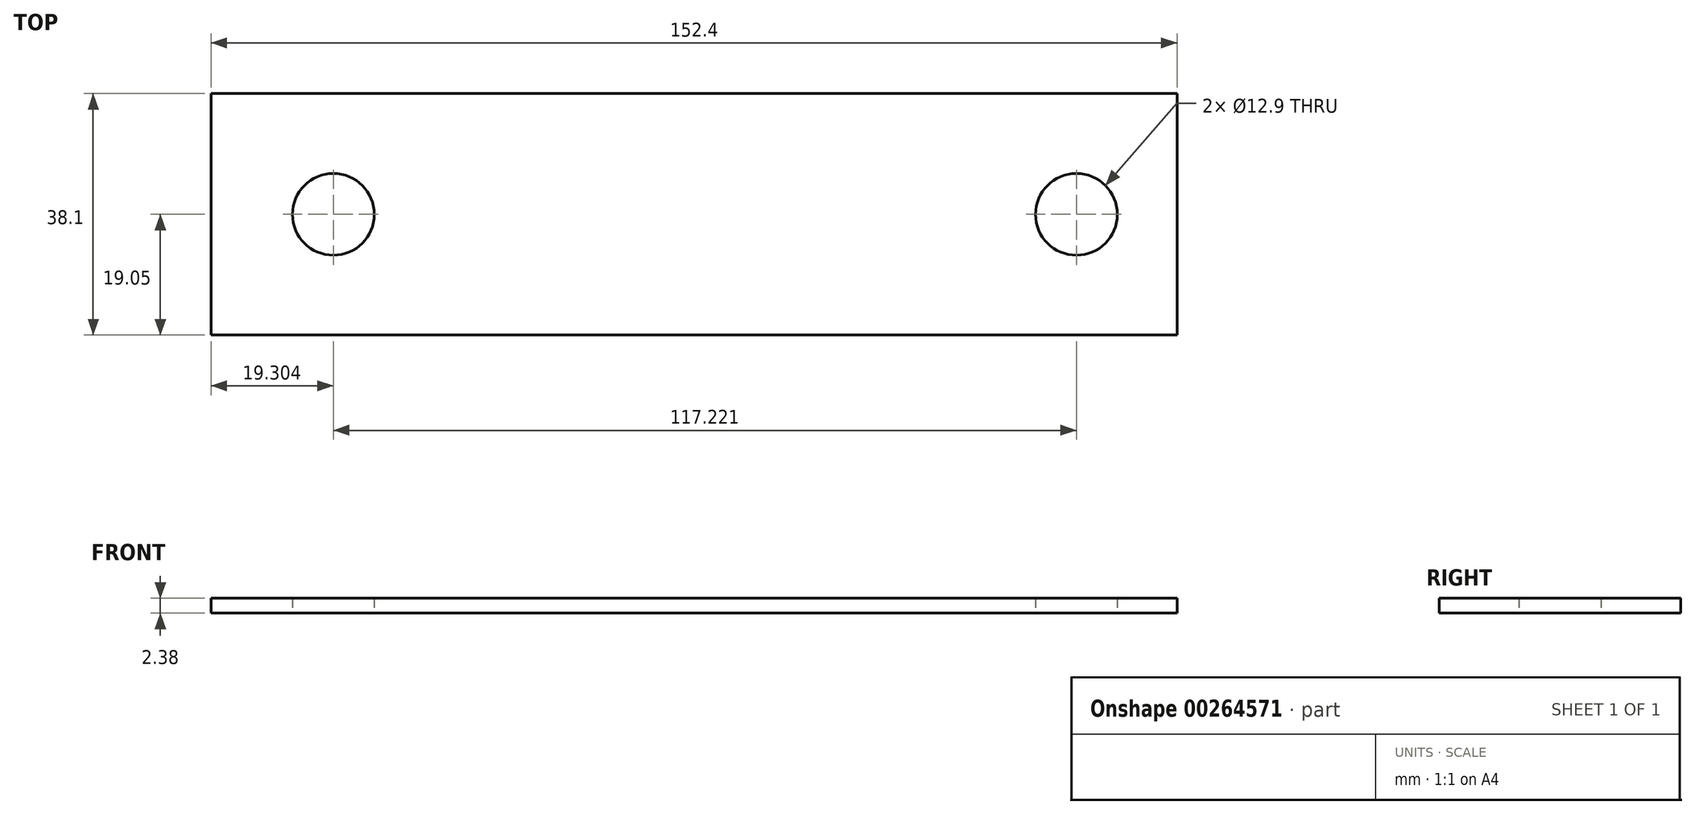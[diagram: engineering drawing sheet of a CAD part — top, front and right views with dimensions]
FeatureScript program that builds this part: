
annotation { "Feature Type Name" : "Feature", "Feature Type Description" : "" }
export const myFeature = defineFeature(function(context is Context, id is Id, definition is map)
    precondition{}
    {
        {
            var Q0;
            Q0=qCreatedBy(makeId("Top.planeOp"),FACE);
            var sketch = newSketch(context, id + "F0", { "sketchPlane" : qUnion([Q0])});
            skLineSegment(sketch, "E0.left", {"start": v(0, 19.05) * mm, "end": v(0, 57.15) * mm});
            skLineSegment(sketch, "E0.right", {"start": v(-152.4, 19.05) * mm, "end": v(-152.4, 57.15) * mm});
            skLineSegment(sketch, "E1", {"start": v(-152.4, 38.1) * mm, "end": v(0, 38.1) * mm});
            skCircle(sketch, "E2", {"center": v(-133.1, 38.1) * mm, "radius": 6.45 * mm});
            skCircle(sketch, "E3", {"center": v(-15.87, 38.1) * mm, "radius": 6.45 * mm});
            skLineSegment(sketch, "E4", {"start": v(-152.4, 19.05) * mm, "end": v(0, 19.05) * mm});
            skLineSegment(sketch, "E5.MirrorCS", {"start": v(-152.4, 57.15) * mm, "end": v(0, 57.15) * mm});
            skPoint(sketch, "E6.orphan", {"position": v(0, 76.2) * mm});
            skPoint(sketch, "E7.orphan", {"position": v(-152.4, 76.2) * mm});
            skPoint(sketch, "E0.bottom.end.orphan", {"position": v(-152.4, 0) * mm});
            skPoint(sketch, "E8.orphan", {"position": v(0, 0) * mm});
            skSolve(sketch);
        }
        {
            var Q0;
            Q0=makeQuery(id+"F0.imprint","IMPRINT",FACE,{"disambiguationData":[TD([[makeQuery(id+"F0.imprint","IMPRINT",EDGE,{"derivedFrom":sQuery(id+"F0.wireOp",EDGE,"E0.bottom")}),-1.0]])]});
            var Q1;
            {var subQ8=sQuery(id+"F0.wireOp",EDGE,"E5.MirrorCS");Q1=makeQuery(id+"F0.imprint","IMPRINT",FACE,{"disambiguationData":[TD([[makeQuery(id+"F0.imprint","IMPRINT",EDGE,{"derivedFrom":subQ8}),-1.0]])]});}
            var Q2;
            {var subQ5=sQuery(id+"F0.wireOp",EDGE,"E4");Q2=makeQuery(id+"F0.imprint","IMPRINT",FACE,{"disambiguationData":[TD([[makeQuery(id+"F0.imprint","IMPRINT",EDGE,{"derivedFrom":subQ5}),1.0]])]});}
            extrude(context, id + "F1", {"entities" : qUnion([Q0, Q1, Q2]), "depth" : 2.38 * mm});
        }
    });
